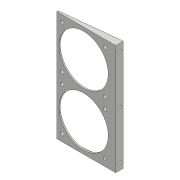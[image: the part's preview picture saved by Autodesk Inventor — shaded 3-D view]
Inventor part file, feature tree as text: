
AUTODESK INVENTOR PART (.ipt)
format: ipt  version: 2018 (Build 220112000, 112)  size: 158,720 bytes
history: native  units: mm
features: sketch x5, extrude x4, mirror x2, hole x2, projected_geometry x2
ambient origin geometry x8: Origin, YZ Plane, XZ Plane, XY Plane, X Axis, Y Axis, Z Axis, Center Point
bodies: Solid1 (feature_tree)
feature tree (15):
  extrude  "Extrusion1"  Depth=100.0mm
  extrude  "Extrusion2"  Depth=7.0mm
  extrude  "Extrusion3"  Depth=1.5mm TaperAngle=0.0deg
  mirror  "Mirror1"
  hole  "Hole1"  [1 undecoded]
  sketch  "Sketch5"  dims[d10=2.4mm d11=6.0mm d12=4.4mm d13=2.0mm d14=90.0deg d15=8.0mm d16=20.594885mm d17=46.0mm d18=40.0mm d19=40.0mm d20=25.0mm d21=25.0mm d22=10.0mm d23=0.0mm d24=3.2mm d25=6.0mm d26=6.3mm d27=2.0mm d28=90.0deg d29=8.0mm d30=20.594885mm]
  extrude  "Extrusion4"  Depth=2.0mm
  hole  "Hole2"  [1 undecoded]
  mirror  "Mirror2"
  sketch  "Sketch1"  dims[d0=53.0mm d1=100.0mm]
  sketch  "Sketch2"  dims[d2=1.2mm d3=0.0mm d4=7.0mm]
  sketch  "Sketch3"  dims[d5=2.0mm d6=0.0mm d7=1.5mm d8=0.0mm]
  projected_geometry  "Projected Loop1"
  sketch  "Sketch4"  dims[d9=90.0mm]
  projected_geometry  "Projected Loop2"
note: 2 required parameter values undecoded (feature->parameter linkage not recoverable at this tier; creation-order binding heuristic only, values carry confidence <= 0.55)
